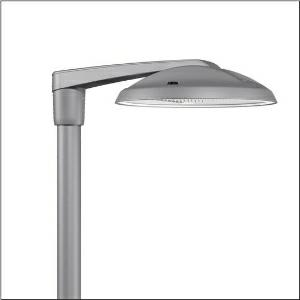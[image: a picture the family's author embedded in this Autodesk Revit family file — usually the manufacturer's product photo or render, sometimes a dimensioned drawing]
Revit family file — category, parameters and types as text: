
# Revit family: dl_r__50_mini___st1_0a_5xa248d33s08ne_6be7
name_source: partatom
category: Lighting Fixtures
units: mm (PartAtom-declared; Revit-internal decimal feet)

## family parameters
Cut with Voids When Loaded = No
Host = Face
Light Source = No
Part Type = Normal
Room Calculation Point = No
Round Connector Dimension = Use Diameter
Shared = No

## types (1)
- --- (1 x LED, 17540 lm, 112.1 W, 3000K)
    Apparent Load = 112 VA
    CIE Flux Codes = 37 72 97 100 100
    Color Rendering = 70
    Color Temperature = 3000K
    Default Elevation = 1800 mm
    Description = DL® 50 mini, mast luminaire, primary light control with lens, of PMMA, primary optical cover: cover, of toughened safety glass, transparent, light distribution: ST1.0a, light emission: direct distribution, primary light characteristic: asymmetric, installation type: post-top, side-entry, LED, High Power LED, rated luminous flux: 17.540lm, luminous efficacy: 156lm/W, light colour: 730, colour temperature: 3000K, control gear: D4i, control: overheat protection, constant luminous flux control, time-dependent luminous flux control, flexible luminous flux parameterisation, mains connection: 230..240V, AC, 50/60Hz, connection cable pre-assembled, cable length: 10,5m, start of lifetime: 112W, end of service life: 118W, reduction: 53W, luminaire housing, of diecast aluminium, powder-coated, Siteco® metallic grey (DB 702S), inclination adjustable: 0°, 5°, 10° (post-top) | 0°, -5°, -10°, -15° (side-entry), please order mast post-top element or mast side-entry element separately, diameter: 500mm, height: 115mm, post-top: for spigot size d x l = 76 x 100mm; with reducer (optional accessory) 60 x 100mm | side-entry: for spigot size d x l = 60 x 100mm; with reducer (optional accessory) 42 x 100mm, mounting height: 4..6m, Smart Interface above, protection rating (complete): IP66, insulation class (complete): insulation class II (safety insulation), certification: CE, ENEC, ENEC+, VDE, impact resistance: IK08, permissible operating ambient temperature for outdoor applications: -25..+40°C, standard-compliant lighting for roads and squares, packaging unit: 1 piece

Light Distribution: ST1.0a
    Height = 115 mm
    Lamp = 1 x LED
    Lamp Light Flux = 17540 lm
    Lamp Power = 112.1 W
    Lamp count = 1
    Length = 500 mm
    Luminous efficacy = 156 lm/W
    Manufacturer = Siteco
    ModVariant = No
    Model = 5XA248D33S08NE
    Number of Poles = 1
    OnlyDefault = Yes
    Power Factor = 1
    Product Name = DL® 50 mini | ST1.0a
    Product group = mast luminaire | pylon top
    ProductGroupID = 6100
    Protection Class = Protection class II
    Protection Degree = IP 66
    RLX_Detail_Level = 1
    RLX_Emergency_Light_Flux = 0 lm
    RLX_Emergency_Type = 0
    RLX_Emergency_Type_DB = No
    RlxData = <blob elided: 106129 chars, md5=4741583c>
    Socket = socket
    Standby Power = 0 W
    System Light Flux = 17540 lm
    System Power = 112 W
    Type Comments = factory setting: luminous flux: 100 % | dim-lin: 254 | 601 mA
    Type Image = l_1251788.jpg
    URL = http://relux.com
    VarID = @adj_065144
    Voltage = 0 V
    Weight = 0.00 kg
    Width = 0 mm  [stored 0 ft]

note: [stored X ft] marks values corroborated as IEEE doubles in the binary element streams (Revit-internal decimal feet)

## geometry (parser evidence)
native form markers: Blend x4, Sweep x10
no freeform markers — native parametric forms only
